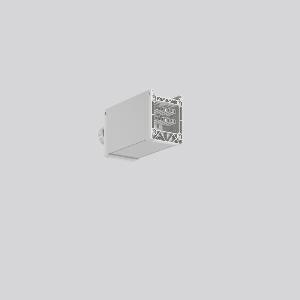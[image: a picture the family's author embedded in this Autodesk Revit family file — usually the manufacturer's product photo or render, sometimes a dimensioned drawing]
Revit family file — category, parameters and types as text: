
# Revit family: linedo_anfangseinspeisung_982859_000_6059
name_source: partatom
category: Lighting Fixtures
units: mm (PartAtom-declared; Revit-internal decimal feet)

## family parameters
Cut with Voids When Loaded = No
Host = Face
Light Source = No
Part Type = Normal
Room Calculation Point = No
Round Connector Dimension = Use Diameter
Shared = No

## types (1)
- LINEDO Anfangseinspeisung
    Apparent Load = 0 VA
    Default Elevation = 1800 mm
    Description = Series: LINEDO
Initial power feed (short Version), 7-pole, connection socket. Housing: extruded aluminium profile, anodised. Cover made of plastic, surface like housing. LINEDO plug system, plastic, light grey. 1 cable gland (M25). Cable gland on side or on top. Convenient connection with flat connector.
Colour: anodised aluminium
Length: 134 mm
Width: 58 mm
Height: 76 mm
Weight: 278 g
    Height = 76 mm
    Lamp = 0 x
    Length = 134 mm
    Luminous efficacy = 0 lm/W
    Manufacturer = RZB
    ModVariant = No
    Model = 982859.000
    Mounting Place = Ceiling
    Mounting Type = Surface mounted
    Number of Poles = 1
    OnlyDefault = Yes
    Power Factor = 1
    Product Name = LINEDO Anfangseinspeisung
    Product group = Surface mounted continuous line luminaire system
    ProductGroupID = 310
    Protection Class = Protection class I
    Protection Degree = Degree of protection
    RLX_Detail_Level = 1
    RLX_Emergency_Light_Flux = 0 lm
    RLX_Emergency_Type = 0
    RLX_Emergency_Type_DB = No
    RlxData = <blob elided: 13193 chars, md5=cd7a994a>
    Standby Power = 0 W
    System Light Flux = 0 lm
    System Power = 0 W
    Type Comments = Product without accessories
    Type Image = 982859.000.jpg
    URL = http://relux.com
    VarID = ---
    Voltage = 0 V
    Weight = 0.00 kg
    Width = 58 mm

## geometry (parser evidence)
native form markers: Sweep x8
no freeform markers — native parametric forms only
